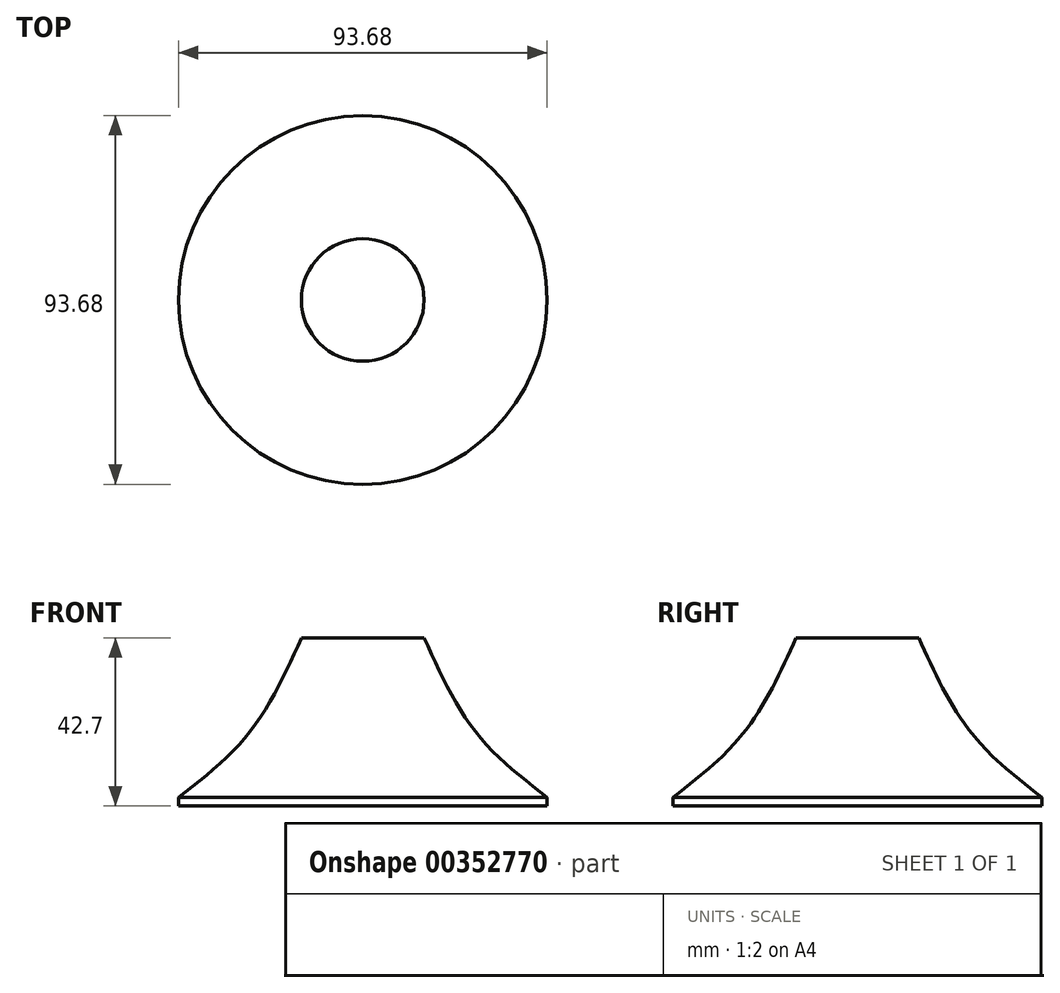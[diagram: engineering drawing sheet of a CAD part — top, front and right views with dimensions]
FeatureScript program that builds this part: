
annotation { "Feature Type Name" : "Feature", "Feature Type Description" : "" }
export const myFeature = defineFeature(function(context is Context, id is Id, definition is map)
    precondition{}
    {
        {
            var Q0;
            Q0=qCreatedBy(makeId("Top.planeOp"),FACE);
            var sketch = newSketch(context, id + "F0", { "sketchPlane" : qUnion([Q0])});
            skCircle(sketch, "E0", {"center": v(0, 0) * mm, "radius": 46.84 * mm});
            skSolve(sketch);
        }
        {
            var Q0;
            Q0=makeQuery(id+"F0.imprint","IMPRINT",FACE,{"disambiguationData":[TD([[makeQuery(id+"F0.imprint","IMPRINT",EDGE,{"derivedFrom":sQuery(id+"F0.wireOp",EDGE,"E0")}),1.0]])]});
            extrude(context, id + "F1", {"entities" : qUnion([Q0]), "depth" : 2.2 * mm});
        }
        {
            var Q0;
            Q0=makeQuery(id+"F1.opExtrude","CAP_FACE",FACE,{"disambiguationData":[OSD([sQuery(id+"F0.wireOp",EDGE,"E0")])],"isStart":false});
            cPlane(context, id + "F2", {"entities" : qUnion([Q0]), "cplaneType" : CPlaneType.OFFSET, "offset" : 14.9 * mm, "width" : 150 * mm, "height" : 150 * mm});
        }
        {
            var Q0;
            Q0=qCreatedBy(id+"F2.planeOp",FACE);
            var sketch = newSketch(context, id + "F3", { "sketchPlane" : qUnion([Q0])});
            skCircle(sketch, "E1", {"center": v(0, 0) * mm, "radius": 30.07 * mm});
            skSolve(sketch);
        }
        {
            var Q0;
            Q0=makeQuery(id+"F1.opExtrude","CAP_FACE",FACE,{"disambiguationData":[OSD([sQuery(id+"F0.wireOp",EDGE,"E0")])],"isStart":false});
            cPlane(context, id + "F4", {"entities" : qUnion([Q0]), "cplaneType" : CPlaneType.OFFSET, "offset" : 40.5 * mm, "width" : 150 * mm, "height" : 150 * mm});
        }
        {
            var Q0;
            Q0=qCreatedBy(id+"F4.planeOp",FACE);
            var sketch = newSketch(context, id + "F5", { "sketchPlane" : qUnion([Q0])});
            skCircle(sketch, "E2", {"center": v(0, 0) * mm, "radius": 15.57 * mm});
            skSolve(sketch);
        }
        {
            var Q0;
            Q0=makeQuery(id+"F1.opExtrude","CAP_FACE",FACE,{"disambiguationData":[OSD([sQuery(id+"F0.wireOp",EDGE,"E0")])],"isStart":false});
            var Q1;
            Q1=makeQuery(id+"F3.imprint","IMPRINT",FACE,{"disambiguationData":[TD([[makeQuery(id+"F3.imprint","IMPRINT",EDGE,{"derivedFrom":sQuery(id+"F3.wireOp",EDGE,"E1")}),1.0]])]});
            var Q2;
            Q2=makeQuery(id+"F5.imprint","IMPRINT",FACE,{"disambiguationData":[TD([[makeQuery(id+"F5.imprint","IMPRINT",EDGE,{"derivedFrom":sQuery(id+"F5.wireOp",EDGE,"E2")}),1.0]])]});
            loft(context, id + "F6", {"sheetProfilesArray" : [{ "sheetProfileEntities" : qUnion([Q0]) }, { "sheetProfileEntities" : qUnion([Q1]) }, { "sheetProfileEntities" : qUnion([Q2]) }]});
        }
    });
